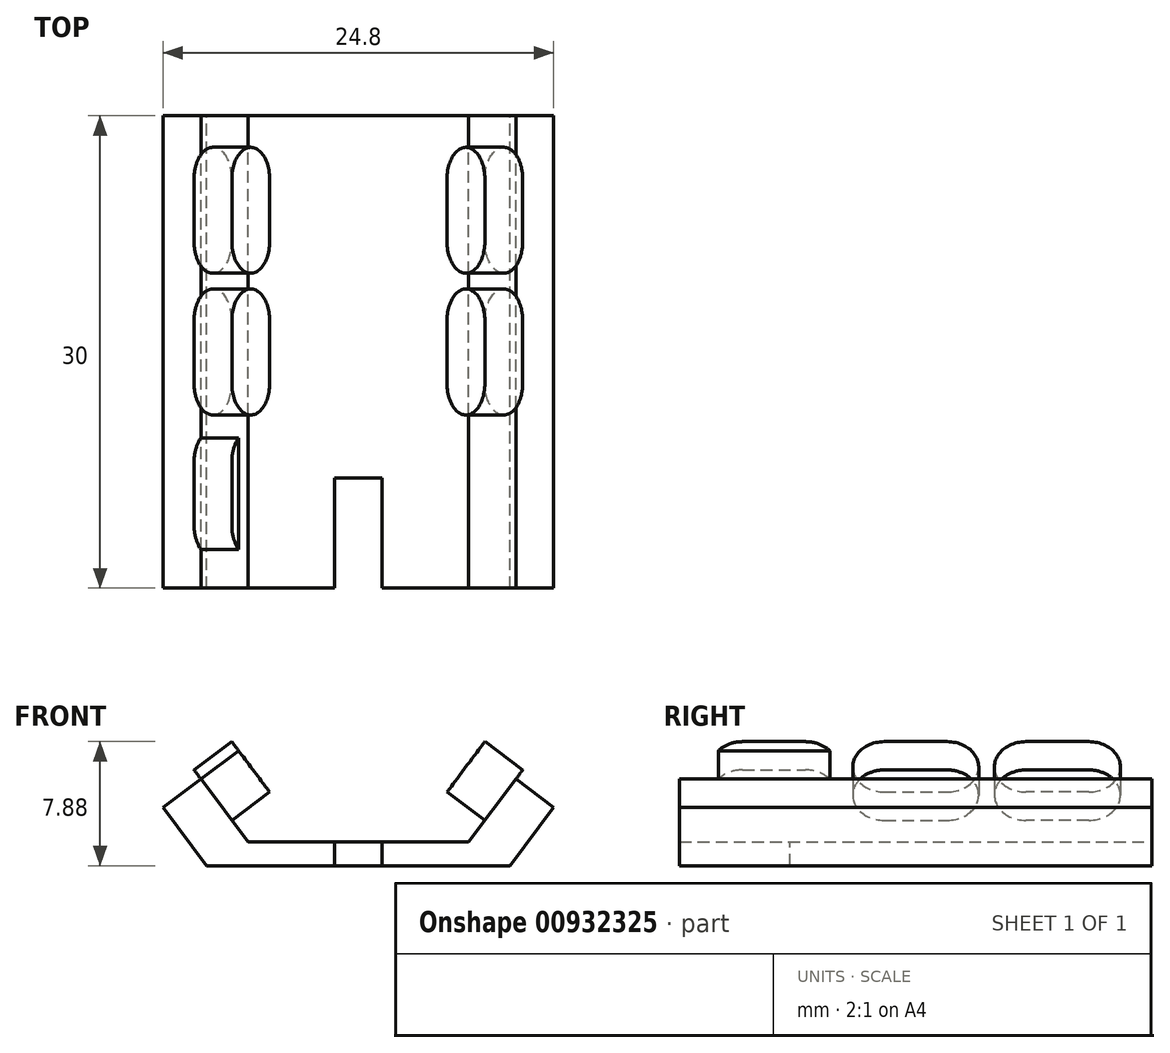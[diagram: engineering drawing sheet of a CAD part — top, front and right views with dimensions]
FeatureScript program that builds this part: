
annotation { "Feature Type Name" : "Feature", "Feature Type Description" : "" }
export const myFeature = defineFeature(function(context is Context, id is Id, definition is map)
    precondition{}
    {
        {
            var Q0;
            Q0=qCreatedBy(makeId("Front.planeOp"),FACE);
            var sketch = newSketch(context, id + "F0", { "sketchPlane" : qUnion([Q0])});
            skLineSegment(sketch, "E0", {"start": v(-9.63, 0) * mm, "end": v(-12.4, 3.7) * mm});
            skLineSegment(sketch, "E1", {"start": v(-12.4, 3.7) * mm, "end": v(-10, 5.5) * mm});
            skLineSegment(sketch, "E2", {"start": v(-10, 5.5) * mm, "end": v(-7, 1.5) * mm});
            skLineSegment(sketch, "E3", {"start": v(-7, 1.5) * mm, "end": v(7, 1.5) * mm});
            skLineSegment(sketch, "E4", {"start": v(7, 1.5) * mm, "end": v(10, 5.5) * mm});
            skLineSegment(sketch, "E5", {"start": v(10, 5.5) * mm, "end": v(12.4, 3.7) * mm});
            skLineSegment(sketch, "E6", {"start": v(12.4, 3.7) * mm, "end": v(9.63, 0) * mm});
            skLineSegment(sketch, "E7", {"start": v(9.63, 0) * mm, "end": v(-9.63, 0) * mm});
            skSolve(sketch);
        }
        {
            var Q0;
            Q0=makeQuery(id+"F0.imprint","IMPRINT",FACE,{"disambiguationData":[TD([[makeQuery(id+"F0.imprint","IMPRINT",EDGE,{"derivedFrom":sQuery(id+"F0.wireOp",EDGE,"E0")}),-1.0]])]});
            extrude(context, id + "F1", {"entities" : qUnion([Q0]), "depth" : 30 * mm, "offsetDistance" : 25.4 * mm});
        }
        {
            var Q0;
            Q0=makeQuery(id+"F1.opExtrude","SWEPT_FACE",FACE,{"disambiguationData":[OSD([sQuery(id+"F0.wireOp",EDGE,"E3")])]});
            var sketch = newSketch(context, id + "F2", { "sketchPlane" : qUnion([Q0])});
            skLineSegment(sketch, "E8.bottom", {"start": v(-1.5, -30) * mm, "end": v(1.5, -30) * mm});
            skLineSegment(sketch, "E8.top", {"start": v(-1.5, -23) * mm, "end": v(1.5, -23) * mm});
            skLineSegment(sketch, "E8.left", {"start": v(-1.5, -30) * mm, "end": v(-1.5, -23) * mm});
            skLineSegment(sketch, "E8.right", {"start": v(1.5, -30) * mm, "end": v(1.5, -23) * mm});
            skSolve(sketch);
        }
        {
            var Q0;
            Q0=makeQuery(id+"F2.imprint","IMPRINT",FACE,{"disambiguationData":[TD([[makeQuery(id+"F2.imprint","IMPRINT",EDGE,{"derivedFrom":sQuery(id+"F2.wireOp",EDGE,"E8.bottom")}),1.0]])]});
            extrude(context, id + "F3", {"entities" : qUnion([Q0]), "operationType" : NewBodyOperationType.REMOVE, "oppositeDirection" : true, "depth" : 25.4 * mm, "offsetDistance" : 25.4 * mm});
        }
        {
            var Q0;
            Q0=makeQuery(id+"F1.opExtrude","SWEPT_FACE",FACE,{"disambiguationData":[OSD([sQuery(id+"F0.wireOp",EDGE,"E2")])]});
            var sketch = newSketch(context, id + "F4", { "sketchPlane" : qUnion([Q0])});
            skLineSegment(sketch, "E9.bottom", {"start": v(-26, 11.12) * mm, "end": v(-22, 11.12) * mm});
            skLineSegment(sketch, "E9.top", {"start": v(-26, 7.12) * mm, "end": v(-22, 7.12) * mm});
            skArc(sketch, "E10", {"start": v(-26, 11.12) * mm, "mid": v(-28, 9.12) * mm, "end": v(-26, 7.12) * mm});
            skArc(sketch, "E11", {"start": v(-22, 7.12) * mm, "mid": v(-20, 9.12) * mm, "end": v(-22, 11.12) * mm});
            skArc(sketch, "E12", {"start": v(-17, 11.12) * mm, "mid": v(-19, 9.12) * mm, "end": v(-17, 7.12) * mm});
            skArc(sketch, "E13", {"start": v(-13, 7.12) * mm, "mid": v(-11, 9.12) * mm, "end": v(-13, 11.12) * mm});
            skLineSegment(sketch, "E14", {"start": v(-17, 11.12) * mm, "end": v(-13, 11.12) * mm});
            skLineSegment(sketch, "E15", {"start": v(-17, 7.12) * mm, "end": v(-13, 7.12) * mm});
            skLineSegment(sketch, "E16", {"start": v(-26, 9.12) * mm, "end": v(-17, 9.12) * mm, "construction": true});
            skArc(sketch, "E17", {"start": v(-8, 11.12) * mm, "mid": v(-10, 9.12) * mm, "end": v(-8, 7.12) * mm});
            skArc(sketch, "E18", {"start": v(-4, 7.12) * mm, "mid": v(-2, 9.12) * mm, "end": v(-4, 11.12) * mm});
            skLineSegment(sketch, "E19", {"start": v(-8, 11.12) * mm, "end": v(-4, 11.12) * mm});
            skLineSegment(sketch, "E20", {"start": v(-4, 7.12) * mm, "end": v(-8, 7.12) * mm});
            skLineSegment(sketch, "E21", {"start": v(-17, 9.12) * mm, "end": v(-8, 9.12) * mm, "construction": true});
            skSolve(sketch);
        }
        {
            var Q0;
            Q0=makeQuery(id+"F4.imprint","IMPRINT",FACE,{"disambiguationData":[TD([[makeQuery(id+"F4.imprint","IMPRINT",EDGE,{"derivedFrom":sQuery(id+"F4.wireOp",EDGE,"E17")}),1.0]])]});
            var Q1;
            Q1=makeQuery(id+"F4.imprint","IMPRINT",FACE,{"disambiguationData":[TD([[makeQuery(id+"F4.imprint","IMPRINT",EDGE,{"derivedFrom":sQuery(id+"F4.wireOp",EDGE,"E12")}),1.0]])]});
            var Q2;
            Q2=makeQuery(id+"F4.imprint","IMPRINT",FACE,{"disambiguationData":[TD([[makeQuery(id+"F4.imprint","IMPRINT",EDGE,{"derivedFrom":sQuery(id+"F4.wireOp",EDGE,"E9.bottom")}),-1.0]])]});
            extrude(context, id + "F5", {"entities" : qUnion([Q0, Q1, Q2]), "operationType" : NewBodyOperationType.ADD, "depth" : 3 * mm, "offsetDistance" : 25.4 * mm});
        }
        {
            var Q0;
            Q0=makeQuery(id+"F1.opExtrude","SWEPT_BODY",BODY,{"disambiguationData":[OSD([sQuery(id+"F0.wireOp",EDGE,"E0"),sQuery(id+"F0.wireOp",EDGE,"E1"),sQuery(id+"F0.wireOp",EDGE,"E2"),sQuery(id+"F0.wireOp",EDGE,"E3"),sQuery(id+"F0.wireOp",EDGE,"E4"),sQuery(id+"F0.wireOp",EDGE,"E5"),sQuery(id+"F0.wireOp",EDGE,"E6"),sQuery(id+"F0.wireOp",EDGE,"E7")])]});
            var Q1;
            Q1=qCreatedBy(makeId("Right.planeOp"),FACE);
            mirror(context, id + "F6", {"operationType" : NewBodyOperationType.ADD, "entities" : qUnion([Q0]), "mirrorPlane" : qUnion([Q1])});
        }
    });
